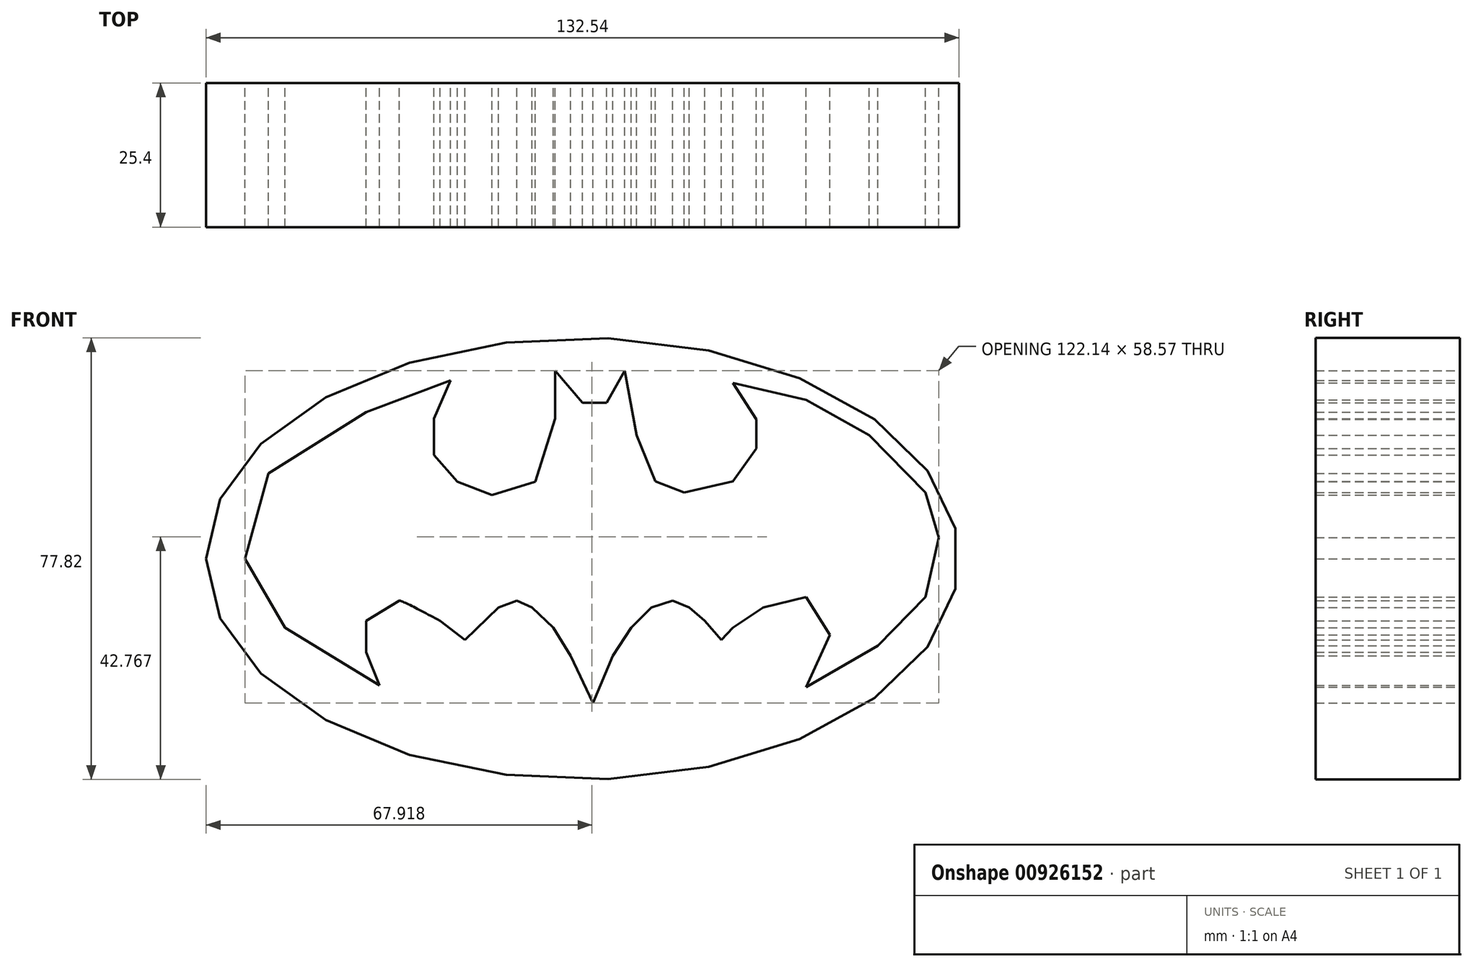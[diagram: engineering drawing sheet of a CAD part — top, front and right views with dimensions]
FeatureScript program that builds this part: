
annotation { "Feature Type Name" : "Feature", "Feature Type Description" : "" }
export const myFeature = defineFeature(function(context is Context, id is Id, definition is map)
    precondition{}
    {
        {
            var Q0;
            Q0=qCreatedBy(makeId("Front.planeOp"),FACE);
            var sketch = newSketch(context, id + "F0", { "sketchPlane" : qUnion([Q0])});
            skFitSpline(sketch, "E0", {"points": [v(-23.21, 31.4) * mm, v(-26.13, 24.67) * mm], "startDerivative": vector(-2.92, -6.72) * mm, "endDerivative": vector(-2.92, -6.72) * mm});
            skFitSpline(sketch, "E1", {"points": [v(-26.13, 24.67) * mm, v(-26.13, 18.25) * mm], "startDerivative": vector(0, -6.42) * mm, "endDerivative": vector(0, -6.42) * mm});
            skFitSpline(sketch, "E2", {"points": [v(-26.13, 18.25) * mm, v(-22.05, 13.58) * mm], "startDerivative": vector(4.09, -4.67) * mm, "endDerivative": vector(4.09, -4.67) * mm});
            skFitSpline(sketch, "E3", {"points": [v(-22.05, 13.58) * mm, v(-15.91, 11.24) * mm], "startDerivative": vector(6.13, -2.34) * mm, "endDerivative": vector(6.13, -2.34) * mm});
            skFitSpline(sketch, "E4", {"points": [v(-15.91, 11.24) * mm, v(-8.32, 13.58) * mm], "startDerivative": vector(7.6, 2.34) * mm, "endDerivative": vector(7.6, 2.34) * mm});
            skFitSpline(sketch, "E5", {"points": [v(-8.32, 13.58) * mm, v(-4.82, 24.67) * mm], "startDerivative": vector(3.5, 11.1) * mm, "endDerivative": vector(3.5, 11.1) * mm});
            skFitSpline(sketch, "E6", {"points": [v(-4.82, 24.67) * mm, v(-4.82, 33.14) * mm], "startDerivative": vector(0, 8.47) * mm, "endDerivative": vector(0, 8.47) * mm});
            skFitSpline(sketch, "E7", {"points": [v(-4.82, 33.14) * mm, v(0, 27.5) * mm], "startDerivative": vector(4.82, -5.65) * mm, "endDerivative": vector(4.82, -5.65) * mm});
            skFitSpline(sketch, "E8", {"points": [v(4.23, 27.5) * mm, v(0, 27.5) * mm], "startDerivative": vector(-4.23, 0) * mm, "endDerivative": vector(-4.23, 0) * mm});
            skFitSpline(sketch, "E9", {"points": [v(4.23, 27.5) * mm, v(7.45, 33.14) * mm], "startDerivative": vector(3.21, 5.65) * mm, "endDerivative": vector(3.21, 5.65) * mm});
            skFitSpline(sketch, "E10", {"points": [v(7.45, 33.14) * mm, v(9.5, 21.75) * mm], "startDerivative": vector(2.04, -11.39) * mm, "endDerivative": vector(2.04, -11.39) * mm});
            skFitSpline(sketch, "E11", {"points": [v(9.5, 21.75) * mm, v(12.8, 13.6) * mm], "startDerivative": vector(3.3, -8.16) * mm, "endDerivative": vector(3.3, -8.16) * mm});
            skFitSpline(sketch, "E12", {"points": [v(12.8, 13.6) * mm, v(17.94, 11.67) * mm], "startDerivative": vector(5.14, -1.93) * mm, "endDerivative": vector(5.14, -1.93) * mm});
            skFitSpline(sketch, "E13", {"points": [v(17.94, 11.67) * mm, v(26.5, 13.6) * mm], "startDerivative": vector(8.57, 1.93) * mm, "endDerivative": vector(8.57, 1.93) * mm});
            skFitSpline(sketch, "E14", {"points": [v(26.5, 13.6) * mm, v(30.58, 19.38) * mm], "startDerivative": vector(4.07, 5.79) * mm, "endDerivative": vector(4.07, 5.79) * mm});
            skFitSpline(sketch, "E15", {"points": [v(30.58, 19.38) * mm, v(30.58, 24.53) * mm], "startDerivative": vector(0, 5.14) * mm, "endDerivative": vector(0, 5.14) * mm});
            skFitSpline(sketch, "E16", {"points": [v(30.58, 24.53) * mm, v(26.5, 30.95) * mm], "startDerivative": vector(-4.07, 6.43) * mm, "endDerivative": vector(-4.07, 6.43) * mm});
            skFitSpline(sketch, "E17", {"points": [v(26.5, 30.95) * mm, v(39.36, 27.96) * mm], "startDerivative": vector(12.86, -3) * mm, "endDerivative": vector(12.86, -3) * mm});
            skFitSpline(sketch, "E18", {"points": [v(39.36, 27.96) * mm, v(50.5, 21.75) * mm], "startDerivative": vector(11.14, -6.2) * mm, "endDerivative": vector(11.14, -6.2) * mm});
            skFitSpline(sketch, "E19", {"points": [v(50.5, 21.75) * mm, v(60.36, 11.67) * mm], "startDerivative": vector(9.86, -10.08) * mm, "endDerivative": vector(9.86, -10.08) * mm});
            skFitSpline(sketch, "E20", {"points": [v(60.36, 11.67) * mm, v(62.72, 3.74) * mm], "startDerivative": vector(2.36, -7.93) * mm, "endDerivative": vector(2.36, -7.93) * mm});
            skFitSpline(sketch, "E21", {"points": [v(62.72, 3.74) * mm, v(60.36, -6.76) * mm], "startDerivative": vector(-2.36, -10.5) * mm, "endDerivative": vector(-2.36, -10.5) * mm});
            skFitSpline(sketch, "E22", {"points": [v(52, -15.33) * mm, v(39.36, -22.61) * mm], "startDerivative": vector(-12.64, -7.29) * mm, "endDerivative": vector(-12.64, -7.29) * mm});
            skFitSpline(sketch, "E23", {"points": [v(39.36, -22.61) * mm, v(43.58, -13.4) * mm], "startDerivative": vector(4.21, 9.21) * mm, "endDerivative": vector(4.21, 9.21) * mm});
            skFitSpline(sketch, "E24", {"points": [v(43.58, -13.4) * mm, v(39.36, -6.76) * mm], "startDerivative": vector(-4.21, 6.64) * mm, "endDerivative": vector(-4.21, 6.64) * mm});
            skFitSpline(sketch, "E25", {"points": [v(60.36, -6.76) * mm, v(52, -15.33) * mm], "startDerivative": vector(-8.36, -8.57) * mm, "endDerivative": vector(-8.36, -8.57) * mm});
            skFitSpline(sketch, "E26", {"points": [v(39.36, -6.76) * mm, v(31.81, -8.57) * mm], "startDerivative": vector(-7.55, -1.82) * mm, "endDerivative": vector(-7.55, -1.82) * mm});
            skFitSpline(sketch, "E27", {"points": [v(31.81, -8.57) * mm, v(26.47, -12.13) * mm], "startDerivative": vector(-5.34, -3.56) * mm, "endDerivative": vector(-5.34, -3.56) * mm});
            skFitSpline(sketch, "E28", {"points": [v(26.47, -12.13) * mm, v(24.41, -14.29) * mm], "startDerivative": vector(-2.06, -2.15) * mm, "endDerivative": vector(-2.06, -2.15) * mm});
            skFitSpline(sketch, "E29", {"points": [v(24.41, -14.29) * mm, v(21.51, -10.92) * mm], "startDerivative": vector(-2.9, 3.37) * mm, "endDerivative": vector(-2.9, 3.37) * mm});
            skFitSpline(sketch, "E30", {"points": [v(21.51, -10.92) * mm, v(18.8, -8.57) * mm], "startDerivative": vector(-2.72, 2.34) * mm, "endDerivative": vector(-2.72, 2.34) * mm});
            skFitSpline(sketch, "E31", {"points": [v(18.8, -8.57) * mm, v(15.9, -7.36) * mm], "startDerivative": vector(-2.9, 1.21) * mm, "endDerivative": vector(-2.9, 1.21) * mm});
            skFitSpline(sketch, "E32", {"points": [v(15.9, -7.36) * mm, v(12.15, -8.57) * mm], "startDerivative": vector(-3.75, -1.21) * mm, "endDerivative": vector(-3.75, -1.21) * mm});
            skFitSpline(sketch, "E33", {"points": [v(12.15, -8.57) * mm, v(8.6, -12.13) * mm], "startDerivative": vector(-3.56, -3.56) * mm, "endDerivative": vector(-3.56, -3.56) * mm});
            skFitSpline(sketch, "E34", {"points": [v(8.6, -12.13) * mm, v(5.31, -17.1) * mm], "startDerivative": vector(-3.28, -4.96) * mm, "endDerivative": vector(-3.28, -4.96) * mm});
            skFitSpline(sketch, "E35", {"points": [v(5.31, -17.1) * mm, v(1.85, -25.43) * mm], "startDerivative": vector(-3.46, -8.33) * mm, "endDerivative": vector(-3.46, -8.33) * mm});
            skFitSpline(sketch, "E36", {"points": [v(1.85, -25.43) * mm, v(-2.08, -17.1) * mm], "startDerivative": vector(-3.93, 8.33) * mm, "endDerivative": vector(-3.93, 8.33) * mm});
            skFitSpline(sketch, "E37", {"points": [v(-2.08, -17.1) * mm, v(-5.17, -12.13) * mm], "startDerivative": vector(-3.09, 4.96) * mm, "endDerivative": vector(-3.09, 4.96) * mm});
            skFitSpline(sketch, "E38", {"points": [v(-5.17, -12.13) * mm, v(-8.92, -8.57) * mm], "startDerivative": vector(-3.75, 3.56) * mm, "endDerivative": vector(-3.75, 3.56) * mm});
            skFitSpline(sketch, "E39", {"points": [v(-8.92, -8.57) * mm, v(-11.54, -7.36) * mm], "startDerivative": vector(-2.62, 1.21) * mm, "endDerivative": vector(-2.62, 1.21) * mm});
            skFitSpline(sketch, "E40", {"points": [v(-11.54, -7.36) * mm, v(-14.82, -8.57) * mm], "startDerivative": vector(-3.28, -1.21) * mm, "endDerivative": vector(-3.28, -1.21) * mm});
            skFitSpline(sketch, "E41", {"points": [v(-14.82, -8.57) * mm, v(-20.72, -14.29) * mm], "startDerivative": vector(-5.9, -5.71) * mm, "endDerivative": vector(-5.9, -5.71) * mm});
            skFitSpline(sketch, "E42", {"points": [v(-20.72, -14.29) * mm, v(-25.12, -10.92) * mm], "startDerivative": vector(-4.4, 3.37) * mm, "endDerivative": vector(-4.4, 3.37) * mm});
            skFitSpline(sketch, "E43", {"points": [v(-25.12, -10.92) * mm, v(-32.27, -7.36) * mm, v(-32.56, -7.36) * mm], "startDerivative": vector(-11.33, 6) * mm, "endDerivative": vector(-1.28, -0.34) * mm});
            skFitSpline(sketch, "E44", {"points": [v(-32.27, -7.36) * mm, v(-38.1, -10.92) * mm], "startDerivative": vector(-5.84, -3.55) * mm, "endDerivative": vector(-5.84, -3.55) * mm});
            skFitSpline(sketch, "E45", {"points": [v(-38.1, -10.92) * mm, v(-38.1, -16.47) * mm], "startDerivative": vector(0, -5.56) * mm, "endDerivative": vector(0, -5.56) * mm});
            skFitSpline(sketch, "E46", {"points": [v(-38.1, -16.47) * mm, v(-35.77, -22.34) * mm], "startDerivative": vector(2.34, -5.87) * mm, "endDerivative": vector(2.34, -5.87) * mm});
            skFitSpline(sketch, "E47", {"points": [v(-35.77, -22.34) * mm, v(-52.42, -12.13) * mm], "startDerivative": vector(-16.64, 10.2) * mm, "endDerivative": vector(-16.64, 10.2) * mm});
            skFitSpline(sketch, "E48", {"points": [v(-52.42, -12.13) * mm, v(-59.42, 0) * mm], "startDerivative": vector(-7, 12.13) * mm, "endDerivative": vector(-7, 12.13) * mm});
            skFitSpline(sketch, "E49", {"points": [v(-59.42, 0) * mm, v(-55.34, 15.04) * mm], "startDerivative": vector(4.09, 15.04) * mm, "endDerivative": vector(4.09, 15.04) * mm});
            skFitSpline(sketch, "E50", {"points": [v(-55.34, 15.04) * mm, v(-38.1, 25.84) * mm], "startDerivative": vector(17.23, 10.8) * mm, "endDerivative": vector(17.23, 10.8) * mm});
            skFitSpline(sketch, "E51", {"points": [v(-38.1, 25.84) * mm, v(-23.21, 31.4) * mm], "startDerivative": vector(14.9, 5.55) * mm, "endDerivative": vector(14.9, 5.55) * mm});
            skEllipse(sketch, "E52", {"center": v(0, 0) * mm, "majorRadius": 66.27 * mm, "minorRadius": 38.9 * mm, "majorAxis": v(-1, 0)});
            skSolve(sketch);
        }
        {
            var Q0;
            Q0 = qSketchRegion(id + "F0", true);
            extrude(context, id + "F1", {"entities" : qUnion([Q0]), "depth" : 25.4 * mm, "offsetDistance" : 25.4 * mm});
        }
    });
